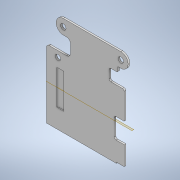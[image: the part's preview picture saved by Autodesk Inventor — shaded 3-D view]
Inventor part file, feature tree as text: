
AUTODESK INVENTOR PART (.ipt)
format: ipt  version: 2022 (Build 260153000, 153)  size: 260,096 bytes
history: native  units: mm
features: reference x13, other x7, extrude x3, sketch x3
ambient origin geometry x8: Origin, YZ Plane, XZ Plane, XY Plane, X Axis, Y Axis, Z Axis, Center Point
bodies: Body1 (feature_tree)
feature tree (26):
  other  "Твердое тело1"
  extrude  "Выдавливание1"  Depth=3.2mm
  extrude  "Выдавливание2"  Depth=3.2mm
  other  "РабПлоскость1"
  extrude  "Выдавливание3"  Depth=3.0mm
  sketch  "Эскиз1"
  reference  "Ссылка1"
  reference  "Ссылка2"
  reference  "Ссылка3"
  reference  "Ссылка4"
  reference  "Ссылка5"
  reference  "Ссылка6"
  reference  "Ссылка7"
  sketch  "Эскиз2"
  reference  "Ссылка9"
  reference  "Ссылка10"
  reference  "Ссылка11"
  reference  "Ссылка13"
  reference  "Ссылка15"
  sketch  "Эскиз3"
  reference  "Ссылка17"
  other  "<userpath>\Documents\Git\MZCAT_2024_construction\MZCAT_2024_RPI_2\MZCAT_4.iam"
  other  "MZCAT_4.iam"
  other  "base:1"
  other  "<userpath>\Documents\Git\MZCAT_2024_construction\MZCAT_2024\MZCAT_4.iam"
  other  "SMT10x2pin:1"
